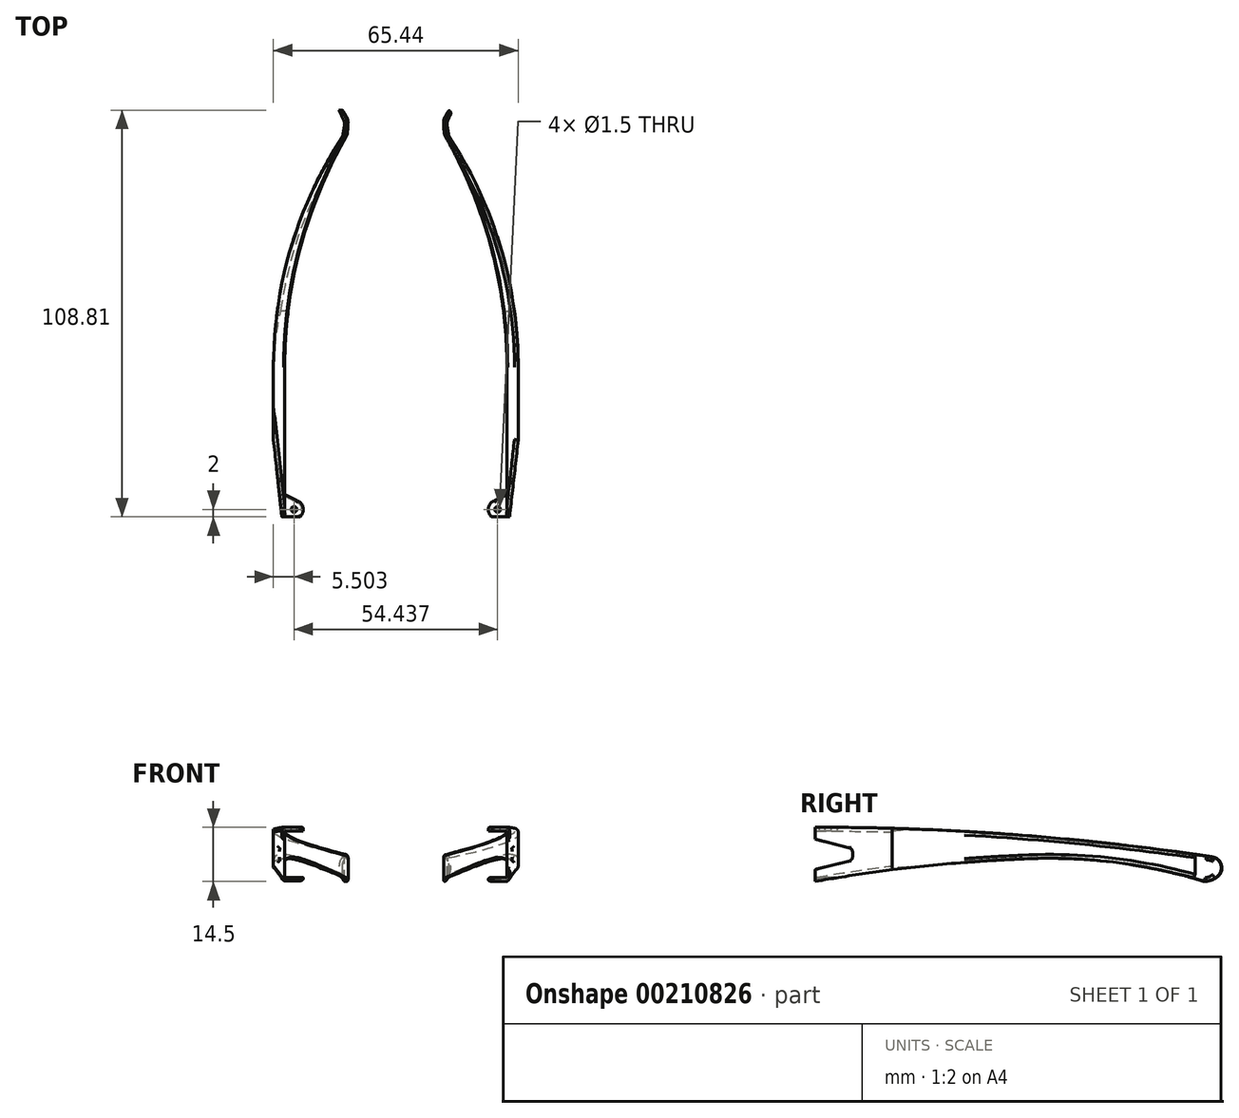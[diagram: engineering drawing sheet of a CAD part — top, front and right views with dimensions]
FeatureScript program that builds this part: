
annotation { "Feature Type Name" : "Feature", "Feature Type Description" : "" }
export const myFeature = defineFeature(function(context is Context, id is Id, definition is map)
    precondition{}
    {
        {
            var Q0;
            Q0=qCreatedBy(makeId("Top.planeOp"),FACE);
            var sketch = newSketch(context, id + "F0", { "sketchPlane" : qUnion([Q0])});
            skLineSegment(sketch, "E0.bottom", {"start": v(-10, 55) * mm, "end": v(10, 55) * mm});
            skLineSegment(sketch, "E0.top", {"start": v(-10, -55) * mm, "end": v(10, -55) * mm});
            skLineSegment(sketch, "E0.left", {"start": v(-10, 55) * mm, "end": v(-10, -55) * mm});
            skLineSegment(sketch, "E0.right", {"start": v(10, 55) * mm, "end": v(10, -55) * mm});
            skPoint(sketch, "E0.middle", {"position": v(0, 0) * mm});
            skSolve(sketch);
        }
        {
            var Q0;
            Q0=makeQuery(id+"F0.imprint","IMPRINT",FACE,{"disambiguationData":[TD([[makeQuery(id+"F0.imprint","IMPRINT",EDGE,{"derivedFrom":sQuery(id+"F0.wireOp",EDGE,"E0.bottom")}),-1.0]])]});
            extrude(context, id + "F1", {"entities" : qUnion([Q0]), "depth" : 14.5 * mm});
        }
        {
            var Q0;
            Q0=makeQuery(id+"F1.opExtrude","SWEPT_FACE",FACE,{"disambiguationData":[OSD([sQuery(id+"F0.wireOp",EDGE,"E0.right")])]});
            var sketch = newSketch(context, id + "F2", { "sketchPlane" : qUnion([Q0])});
            skLineSegment(sketch, "E1", {"start": v(-55, 14.5) * mm, "end": v(-55, 11.3) * mm});
            skLineSegment(sketch, "E2", {"start": v(-55, 0) * mm, "end": v(-55, 3.2) * mm});
            skLineSegment(sketch, "E3", {"start": v(-44.97, 6.5) * mm, "end": v(-44.97, 7.97) * mm});
            skLineSegment(sketch, "E4", {"start": v(-45.72, 8.93) * mm, "end": v(-55, 11.3) * mm});
            skLineSegment(sketch, "E5", {"start": v(-45.73, 5.52) * mm, "end": v(-55, 3.2) * mm});
            skPoint(sketch, "E6.visualSharp", {"position": v(-44.97, 8.74) * mm});
            skArc(sketch, "E6.filletArc", {"start": v(-44.97, 7.97) * mm, "mid": v(-45.18, 8.58) * mm, "end": v(-45.72, 8.93) * mm});
            skPoint(sketch, "E7.visualSharp", {"position": v(-44.97, 5.71) * mm});
            skArc(sketch, "E7.filletArc", {"start": v(-45.73, 5.52) * mm, "mid": v(-45.18, 5.88) * mm, "end": v(-44.97, 6.5) * mm});
            skLineSegment(sketch, "E8", {"start": v(55, 0) * mm, "end": v(55, 6) * mm});
            skLineSegment(sketch, "E9", {"start": v(55, 14.5) * mm, "end": v(55, 0) * mm});
            skLineSegment(sketch, "E10", {"start": v(55, 0) * mm, "end": v(49, 0) * mm});
            skArc(sketch, "E11", {"start": v(49, 0) * mm, "mid": v(50.9, 0.31) * mm, "end": v(52.62, 1.21) * mm});
            skArc(sketch, "E12", {"start": v(51.25, 6.57) * mm, "mid": v(-1.73, 12.52) * mm, "end": v(-55, 14.5) * mm});
            skPoint(sketch, "E13.endSnap0", {"position": v(0, 0) * mm});
            skArc(sketch, "E14", {"start": v(0, 6) * mm, "mid": v(-27.6, 3.9) * mm, "end": v(-55, 0) * mm});
            skArc(sketch, "E15", {"start": v(49, 0) * mm, "mid": v(24.76, 5.15) * mm, "end": v(0, 6) * mm});
            skPoint(sketch, "E16.visualSharp", {"position": v(55, 6) * mm});
            skArc(sketch, "E16.filletArc", {"start": v(52.62, 1.21) * mm, "mid": v(53.72, 4.34) * mm, "end": v(51.25, 6.57) * mm});
            skLineSegment(sketch, "E17", {"start": v(-55, 11.3) * mm, "end": v(-55, 3.2) * mm});
            skLineSegment(sketch, "E18", {"start": v(-55, 14.5) * mm, "end": v(55, 14.5) * mm});
            skSolve(sketch);
        }
        {
            var Q0;
            {var subQ0=sQuery(id+"F2.wireOp",EDGE,"E14");Q0=makeQuery(id+"F2.imprint","IMPRINT",FACE,{"disambiguationData":[TD([[makeQuery(id+"F2.imprint","IMPRINT",EDGE,{"derivedFrom":subQ0}),1.0]])]});}
            extrude(context, id + "F3", {"entities" : qUnion([Q0]), "operationType" : NewBodyOperationType.REMOVE, "oppositeDirection" : true, "depth" : 25 * mm});
        }
        {
            var Q0;
            Q0=makeQuery(id+"F2.imprint","IMPRINT",FACE,{"disambiguationData":[TD([[makeQuery(id+"F2.imprint","IMPRINT",EDGE,{"derivedFrom":sQuery(id+"F2.wireOp",EDGE,"E3")}),1.0]])]});
            extrude(context, id + "F4", {"entities" : qUnion([Q0]), "operationType" : NewBodyOperationType.REMOVE, "oppositeDirection" : true, "depth" : 25 * mm});
        }
        {
            var Q0;
            {var subQ0=sQuery(id+"F2.wireOp",EDGE,"E10");Q0=makeQuery(id+"F2.imprint","IMPRINT",FACE,{"disambiguationData":[TD([[makeQuery(id+"F2.imprint","IMPRINT",EDGE,{"derivedFrom":subQ0}),-1.0]])]});}
            extrude(context, id + "F5", {"entities" : qUnion([Q0]), "operationType" : NewBodyOperationType.REMOVE, "oppositeDirection" : true, "depth" : 25 * mm});
        }
        {
            var Q0;
            Q0=qCreatedBy(makeId("Top.planeOp"),FACE);
            var Q1;
            Q1=sQuery(id+"F2.wireOp",VERTEX,"E12.end");
            cPlane(context, id + "F6", {"entities" : qUnion([Q0, Q1]), "cplaneType" : CPlaneType.PLANE_POINT, "offset" : 25 * mm, "width" : 150 * mm, "height" : 150 * mm});
        }
        {
            var Q0;
            Q0=qCreatedBy(id+"F6.planeOp",FACE);
            var sketch = newSketch(context, id + "F7", { "sketchPlane" : qUnion([Q0])});
            skLineSegment(sketch, "E19.0", {"start": v(-10, 53.8) * mm, "end": v(-10, -55) * mm});
            skLineSegment(sketch, "E20.0", {"start": v(10, -55) * mm, "end": v(10, 55) * mm});
            skLineSegment(sketch, "E21", {"start": v(10, -55) * mm, "end": v(10, -15) * mm});
            skArc(sketch, "E22", {"start": v(10, -15) * mm, "mid": v(5.28, 17.16) * mm, "end": v(-8.48, 46.61) * mm});
            skLineSegment(sketch, "E23", {"start": v(10, -55) * mm, "end": v(7, -55) * mm});
            skLineSegment(sketch, "E24", {"start": v(7, -55) * mm, "end": v(7, -15) * mm});
            skArc(sketch, "E25", {"start": v(7, -15) * mm, "mid": v(2.83, 16.88) * mm, "end": v(-9.4, 46.62) * mm});
            skLineSegment(sketch, "E26", {"start": v(-9.94, 50.34) * mm, "end": v(-9.8, 47.93) * mm});
            skPoint(sketch, "E27.visualSharp", {"position": v(-9.75, 47.22) * mm});
            skArc(sketch, "E27.filletArc", {"start": v(-9.8, 47.93) * mm, "mid": v(-9.67, 47.25) * mm, "end": v(-9.4, 46.62) * mm});
            skLineSegment(sketch, "E28", {"start": v(-10, 53.8) * mm, "end": v(10, 53.8) * mm});
            skLineSegment(sketch, "E29", {"start": v(-10, 53.8) * mm, "end": v(-8.5, 53.8) * mm});
            skLineSegment(sketch, "E30", {"start": v(-8.5, 53.8) * mm, "end": v(-9.54, 52.04) * mm});
            skPoint(sketch, "E31.visualSharp", {"position": v(-10, 51.25) * mm});
            skArc(sketch, "E31.filletArc", {"start": v(-9.54, 52.04) * mm, "mid": v(-9.87, 51.22) * mm, "end": v(-9.94, 50.34) * mm});
            skLineSegment(sketch, "E32", {"start": v(-8.5, 53.8) * mm, "end": v(-7.5, 53.8) * mm});
            skLineSegment(sketch, "E33", {"start": v(-7.5, 53.8) * mm, "end": v(-8.7, 51.33) * mm});
            skLineSegment(sketch, "E34", {"start": v(-8.97, 49.52) * mm, "end": v(-8.48, 46.61) * mm});
            skPoint(sketch, "E35.visualSharp", {"position": v(-9.13, 50.47) * mm});
            skArc(sketch, "E35.filletArc", {"start": v(-8.7, 51.33) * mm, "mid": v(-8.98, 50.45) * mm, "end": v(-8.97, 49.52) * mm});
            skLineSegment(sketch, "E36.0.0", {"start": v(-10, 51.25) * mm, "end": v(-10, -55) * mm});
            skLineSegment(sketch, "E36.0.1", {"start": v(-10, -55) * mm, "end": v(10, -55) * mm});
            skLineSegment(sketch, "E36.0.2", {"start": v(10, -55) * mm, "end": v(10, 51.25) * mm});
            skSolve(sketch);
        }
        {
            var Q0;
            {var subQ0=sQuery(id+"F7.wireOp",EDGE,"E22");Q0=makeQuery(id+"F7.imprint","IMPRINT",FACE,{"disambiguationData":[TD([[makeQuery(id+"F7.imprint","IMPRINT",EDGE,{"derivedFrom":subQ0}),-1.0]])]});}
            extrude(context, id + "F8", {"entities" : qUnion([Q0]), "operationType" : NewBodyOperationType.REMOVE, "oppositeDirection" : true, "depth" : 25 * mm});
        }
        {
            var Q0;
            Q0=makeQuery(id+"F7.imprint","IMPRINT",FACE,{"disambiguationData":[TD([[makeQuery(id+"F7.imprint","IMPRINT",EDGE,{"derivedFrom":sQuery(id+"F7.wireOp",EDGE,"E19.0")}),1.0]])]});
            extrude(context, id + "F9", {"entities" : qUnion([Q0]), "operationType" : NewBodyOperationType.REMOVE, "oppositeDirection" : true, "depth" : 25 * mm});
        }
        {
            var Q0;
            Q0=qCreatedBy(makeId("Top.planeOp"),FACE);
            var sketch = newSketch(context, id + "F10", { "sketchPlane" : qUnion([Q0])});
            skArc(sketch, "E37.0", {"start": v(3.71, -50.63) * mm, "mid": v(2.03, -52.6) * mm, "end": v(3, -55) * mm});
            skLineSegment(sketch, "E38.0", {"start": v(3.71, -50.63) * mm, "end": v(7, -49.01) * mm});
            skLineSegment(sketch, "E39.0", {"start": v(7, -49.01) * mm, "end": v(7, -55) * mm});
            skLineSegment(sketch, "E40.0", {"start": v(3, -55) * mm, "end": v(7, -55) * mm});
            skPoint(sketch, "E41.orphan", {"position": v(-10, -55) * mm});
            skPoint(sketch, "E42.orphan", {"position": v(10, -55) * mm});
            skCircle(sketch, "E43.0", {"center": v(4.5, -53) * mm, "radius": 0.75 * mm});
            skSolve(sketch);
        }
        {
            var Q0;
            Q0=makeQuery(id+"F10.imprint","IMPRINT",FACE,{"disambiguationData":[TD([[makeQuery(id+"F10.imprint","IMPRINT",EDGE,{"derivedFrom":sQuery(id+"F10.wireOp",EDGE,"E37.0")}),1.0]])]});
            extrude(context, id + "F11", {"entities" : qUnion([Q0]), "operationType" : NewBodyOperationType.ADD, "depth" : 1 * mm});
        }
        {
            var Q0;
            {var subQ0=sQuery(id+"F2.wireOp",EDGE,"E14");Q0=makeQuery(id+"F2.imprint","IMPRINT",FACE,{"disambiguationData":[TD([[makeQuery(id+"F2.imprint","IMPRINT",EDGE,{"derivedFrom":subQ0}),1.0]])]});}
            extrude(context, id + "F12", {"entities" : qUnion([Q0]), "operationType" : NewBodyOperationType.REMOVE, "oppositeDirection" : true, "depth" : 25 * mm});
        }
        {
            var Q0;
            {var subQ0=sQuery(id+"F2.wireOp",EDGE,"E10");Q0=makeQuery(id+"F2.imprint","IMPRINT",FACE,{"disambiguationData":[TD([[makeQuery(id+"F2.imprint","IMPRINT",EDGE,{"derivedFrom":subQ0}),-1.0]])]});}
            extrude(context, id + "F13", {"entities" : qUnion([Q0]), "operationType" : NewBodyOperationType.REMOVE, "oppositeDirection" : true, "depth" : 25 * mm});
        }
        {
            var Q0;
            Q0=qCreatedBy(makeId("Top.planeOp"),FACE);
            var Q1;
            Q1=sQuery(id+"F7.wireOp",VERTEX,"E24.start");
            cPlane(context, id + "F14", {"entities" : qUnion([Q0, Q1]), "cplaneType" : CPlaneType.PLANE_POINT, "offset" : 25 * mm, "width" : 150 * mm, "height" : 150 * mm});
        }
        {
            var Q0;
            Q0=qCreatedBy(id+"F14.planeOp",FACE);
            var sketch = newSketch(context, id + "F15", { "sketchPlane" : qUnion([Q0])});
            skLineSegment(sketch, "E44.0", {"start": v(7, -55) * mm, "end": v(7, -49.01) * mm});
            skLineSegment(sketch, "E45.0", {"start": v(3.71, -50.63) * mm, "end": v(7, -49.01) * mm});
            skArc(sketch, "E46.0", {"start": v(3.71, -50.63) * mm, "mid": v(2.03, -52.6) * mm, "end": v(3, -55) * mm});
            skCircle(sketch, "E47.0", {"center": v(4.5, -53) * mm, "radius": 0.75 * mm});
            skLineSegment(sketch, "E48.0", {"start": v(3, -55) * mm, "end": v(7, -55) * mm});
            skPoint(sketch, "E49.orphan", {"position": v(6.85, -49.09) * mm});
            skPoint(sketch, "E50.orphan", {"position": v(7, -15) * mm});
            skPoint(sketch, "E51.orphan", {"position": v(-10, -55) * mm});
            skPoint(sketch, "E52.orphan", {"position": v(10, -55) * mm});
            skSolve(sketch);
        }
        {
            var Q0;
            Q0=makeQuery(id+"F15.imprint","IMPRINT",FACE,{"disambiguationData":[TD([[makeQuery(id+"F15.imprint","IMPRINT",EDGE,{"derivedFrom":sQuery(id+"F15.wireOp",EDGE,"E44.0")}),1.0]])]});
            extrude(context, id + "F16", {"entities" : qUnion([Q0]), "operationType" : NewBodyOperationType.ADD, "oppositeDirection" : true, "depth" : 1 * mm});
        }
        {
            var Q0;
            Q0=makeQuery(id+"F1.opExtrude","SWEPT_BODY",BODY,{"disambiguationData":[OSD([sQuery(id+"F0.wireOp",EDGE,"E0.bottom"),sQuery(id+"F0.wireOp",EDGE,"E0.top"),sQuery(id+"F0.wireOp",EDGE,"E0.left"),sQuery(id+"F0.wireOp",EDGE,"E0.right")])]});
            transform(context, id + "F17", {"entities" : qUnion([Q0]), "transformType" : TransformType.TRANSLATION_3D, "dx" : 0 * mm, "dy" : 0 * mm, "dz" : 0 * mm, "makeCopy" : true});
        }
        {
            var Q0;
            Q0=makeQuery(id+"F17.opPattern","COPY",BODY,{"derivedFrom":makeQuery(id+"F1.opExtrude","SWEPT_BODY",BODY,{"disambiguationData":[OSD([sQuery(id+"F0.wireOp",EDGE,"E0.bottom"),sQuery(id+"F0.wireOp",EDGE,"E0.top"),sQuery(id+"F0.wireOp",EDGE,"E0.left"),sQuery(id+"F0.wireOp",EDGE,"E0.right")])]}),"instanceName":"1"});
            deleteBodies(context, id + "F18", {"entities" : qUnion([Q0])});
        }
        {
            var Q0;
            {var subQ0=sQuery(id+"F7.wireOp",EDGE,"E22");Q0=makeQuery(id+"F7.imprint","IMPRINT",FACE,{"disambiguationData":[TD([[makeQuery(id+"F7.imprint","IMPRINT",EDGE,{"derivedFrom":subQ0}),1.0]])]});}
            var sketch = newSketch(context, id + "F19", { "sketchPlane" : qUnion([Q0])});
            skLineSegment(sketch, "E53.0", {"start": v(-10, -55) * mm, "end": v(10, -55) * mm});
            skLineSegment(sketch, "E54.0", {"start": v(7, -55) * mm, "end": v(7, -15) * mm});
            skLineSegment(sketch, "E55", {"start": v(7, -55) * mm, "end": v(7.7, -55) * mm});
            skLineSegment(sketch, "E56.0", {"start": v(10, -34.38) * mm, "end": v(10, -55) * mm});
            skLineSegment(sketch, "E57", {"start": v(7.7, -55) * mm, "end": v(10, -34.38) * mm});
            skPoint(sketch, "E58.orphan", {"position": v(10, 51.25) * mm});
            skSolve(sketch);
        }
        {
            var Q0;
            Q0 = qSketchRegion(id + "F19", true);
            extrude(context, id + "F20", {"entities" : qUnion([Q0]), "operationType" : NewBodyOperationType.REMOVE, "oppositeDirection" : true, "depth" : 25 * mm});
        }
        {
            var Q0;
            Q0=qCreatedBy(makeId("Top.planeOp"),FACE);
            var sketch = newSketch(context, id + "F21", { "sketchPlane" : qUnion([Q0])});
            skLineSegment(sketch, "E59", {"start": v(-22.72, 54.97) * mm, "end": v(-22.72, -56.62) * mm});
            skSolve(sketch);
        }
        {
            var Q0;
            Q0=qCreatedBy(makeId("Right.planeOp"),FACE);
            var Q1;
            Q1=sQuery(id+"F21.wireOp",VERTEX,"E59.end");
            cPlane(context, id + "F22", {"entities" : qUnion([Q0, Q1]), "cplaneType" : CPlaneType.PLANE_POINT, "offset" : 25 * mm, "width" : 150 * mm, "height" : 150 * mm});
        }
        {
            var Q0;
            Q0=makeQuery(id+"F1.opExtrude","SWEPT_BODY",BODY,{"disambiguationData":[OSD([sQuery(id+"F0.wireOp",EDGE,"E0.bottom"),sQuery(id+"F0.wireOp",EDGE,"E0.top"),sQuery(id+"F0.wireOp",EDGE,"E0.left"),sQuery(id+"F0.wireOp",EDGE,"E0.right")])]});
            var Q1;
            Q1=qCreatedBy(id+"F22.planeOp",FACE);
            mirror(context, id + "F23", {"entities" : qUnion([Q0]), "mirrorPlane" : qUnion([Q1])});
        }
        {
            var Q0;
            Q0=makeQuery(id+"F20.boolean.opBoolean","INTERSECT",EDGE,{"derivedFrom":[makeQuery(id+"F5.boolean.opBoolean","COPY",FACE,{"derivedFrom":makeQuery(id+"F5.opExtrude","SWEPT_FACE",FACE,{"disambiguationData":[OSD([sQuery(id+"F2.wireOp",EDGE,"E12")])]})}),makeQuery(id+"F20.opExtrude","SWEPT_FACE",FACE,{"disambiguationData":[OSD([sQuery(id+"F19.wireOp",EDGE,"E57")])]})]});
            var Q1;
            Q1=makeQuery(id+"F5.boolean.opBoolean","COPY",EDGE,{"derivedFrom":makeQuery(id+"F5.opExtrude","CAP_EDGE",EDGE,{"disambiguationData":[OSD([sQuery(id+"F2.wireOp",EDGE,"E12")])],"isStart":true})});
            var Q2;
            Q2=makeQuery(id+"F8.boolean.opBoolean","INTERSECT",EDGE,{"derivedFrom":[makeQuery(id+"F5.boolean.opBoolean","COPY",FACE,{"derivedFrom":makeQuery(id+"F5.opExtrude","SWEPT_FACE",FACE,{"disambiguationData":[OSD([sQuery(id+"F2.wireOp",EDGE,"E12")])]})}),makeQuery(id+"F8.opExtrude","SWEPT_FACE",FACE,{"disambiguationData":[OSD([sQuery(id+"F7.wireOp",EDGE,"E22")])]})]});
            var Q3;
            {var subQ0=sQuery(id+"F2.wireOp",EDGE,"E14");Q3=makeQuery(id+"F20.boolean.opBoolean","INTERSECT",EDGE,{"derivedFrom":[makeQuery(id+"F12.boolean.opBoolean","MERGE",FACE,{"derivedFrom":[makeQuery(id+"F3.boolean.opBoolean","COPY",FACE,{"derivedFrom":makeQuery(id+"F3.opExtrude","SWEPT_FACE",FACE,{"disambiguationData":[OSD([subQ0])]})}),makeQuery(id+"F12.opExtrude","SWEPT_FACE",FACE,{"disambiguationData":[OSD([subQ0])]})]}),makeQuery(id+"F20.opExtrude","SWEPT_FACE",FACE,{"disambiguationData":[OSD([sQuery(id+"F19.wireOp",EDGE,"E57")])]})]});}
            var Q4;
            Q4=makeQuery(id+"F3.boolean.opBoolean","COPY",EDGE,{"derivedFrom":makeQuery(id+"F3.opExtrude","CAP_EDGE",EDGE,{"disambiguationData":[OSD([sQuery(id+"F2.wireOp",EDGE,"E14")])],"isStart":true})});
            var Q5;
            Q5=makeQuery(id+"F8.boolean.opBoolean","INTERSECT",EDGE,{"derivedFrom":[makeQuery(id+"F3.boolean.opBoolean","COPY",FACE,{"derivedFrom":makeQuery(id+"F3.opExtrude","SWEPT_FACE",FACE,{"disambiguationData":[OSD([sQuery(id+"F2.wireOp",EDGE,"E14")])]})}),makeQuery(id+"F8.opExtrude","SWEPT_FACE",FACE,{"disambiguationData":[OSD([sQuery(id+"F7.wireOp",EDGE,"E22")])]})]});
            var Q6;
            Q6=makeQuery(id+"F8.boolean.opBoolean","INTERSECT",EDGE,{"derivedFrom":[makeQuery(id+"F3.boolean.opBoolean","COPY",FACE,{"derivedFrom":makeQuery(id+"F3.opExtrude","SWEPT_FACE",FACE,{"disambiguationData":[OSD([sQuery(id+"F2.wireOp",EDGE,"E15")])]})}),makeQuery(id+"F8.opExtrude","SWEPT_FACE",FACE,{"disambiguationData":[OSD([sQuery(id+"F7.wireOp",EDGE,"E22")])]})]});
            var Q7;
            Q7=makeQuery(id+"F8.boolean.opBoolean","INTERSECT",EDGE,{"derivedFrom":[makeQuery(id+"F3.boolean.opBoolean","COPY",FACE,{"derivedFrom":makeQuery(id+"F3.opExtrude","SWEPT_FACE",FACE,{"disambiguationData":[OSD([sQuery(id+"F2.wireOp",EDGE,"E15")])]})}),makeQuery(id+"F8.opExtrude","SWEPT_FACE",FACE,{"disambiguationData":[OSD([sQuery(id+"F7.wireOp",EDGE,"E34")])]})]});
            var Q8;
            Q8=makeQuery(id+"F8.boolean.opBoolean","INTERSECT",EDGE,{"derivedFrom":[makeQuery(id+"F5.boolean.opBoolean","COPY",FACE,{"derivedFrom":makeQuery(id+"F5.opExtrude","SWEPT_FACE",FACE,{"disambiguationData":[OSD([sQuery(id+"F2.wireOp",EDGE,"E11")])]})}),makeQuery(id+"F8.opExtrude","SWEPT_FACE",FACE,{"disambiguationData":[OSD([sQuery(id+"F7.wireOp",EDGE,"E34")])]})]});
            var Q9;
            Q9=makeQuery(id+"F8.boolean.opBoolean","INTERSECT",EDGE,{"derivedFrom":[makeQuery(id+"F5.boolean.opBoolean","COPY",FACE,{"derivedFrom":makeQuery(id+"F5.opExtrude","SWEPT_FACE",FACE,{"disambiguationData":[OSD([sQuery(id+"F2.wireOp",EDGE,"E11")])]})}),makeQuery(id+"F8.opExtrude","SWEPT_FACE",FACE,{"disambiguationData":[OSD([sQuery(id+"F7.wireOp",EDGE,"E35.filletArc")])]})]});
            fillet(context, id + "F24", {"entities" : qUnion([Q0, Q1, Q2, Q3, Q4, Q5, Q6, Q7, Q8, Q9]), "radius" : 1 * mm, "tangentPropagation" : true, "allowEdgeOverflow" : false});
        }
        {
            var Q0;
            {var subQ0=makeQuery(id+"F9.opExtrude","SWEPT_FACE",FACE,{"disambiguationData":[OSD([sQuery(id+"F7.wireOp",EDGE,"E24")])]});var subQ1=makeQuery(id+"F5.boolean.opBoolean","COPY",FACE,{"derivedFrom":makeQuery(id+"F5.opExtrude","SWEPT_FACE",FACE,{"disambiguationData":[OSD([sQuery(id+"F2.wireOp",EDGE,"E12")])]})});Q0=makeQuery(id+"F16.boolean.opBoolean","SPLIT",EDGE,{"disambiguationData":[TD([makeQuery(id+"F9.boolean.opBoolean","COPY",FACE,{"derivedFrom":makeQuery(id+"F9.opExtrude","SWEPT_FACE",FACE,{"disambiguationData":[OSD([sQuery(id+"F7.wireOp",EDGE,"E25")])]})})])],"derivedFrom":makeQuery(id+"F9.boolean.opBoolean","INTERSECT",EDGE,{"derivedFrom":[subQ1,subQ0]})});}
            fillet(context, id + "F25", {"entities" : qUnion([Q0]), "radius" : 0.2 * mm, "tangentPropagation" : true, "allowEdgeOverflow" : false});
        }
        {
            var Q0;
            {var subQ1=makeQuery(id+"F9.opExtrude","SWEPT_FACE",FACE,{"disambiguationData":[OSD([sQuery(id+"F7.wireOp",EDGE,"E24")])]});var subQ2=makeQuery(id+"F3.boolean.opBoolean","COPY",FACE,{"derivedFrom":makeQuery(id+"F3.opExtrude","SWEPT_FACE",FACE,{"disambiguationData":[OSD([sQuery(id+"F2.wireOp",EDGE,"E14")])]})});Q0=makeQuery(id+"F11.boolean.opBoolean","SPLIT",EDGE,{"disambiguationData":[TD([makeQuery(id+"F9.boolean.opBoolean","COPY",FACE,{"derivedFrom":makeQuery(id+"F9.opExtrude","SWEPT_FACE",FACE,{"disambiguationData":[OSD([sQuery(id+"F7.wireOp",EDGE,"E25")])]})})])],"derivedFrom":makeQuery(id+"F9.boolean.opBoolean","INTERSECT",EDGE,{"derivedFrom":[subQ2,subQ1]})});}
            var Q1;
            Q1=makeQuery(id+"F9.boolean.opBoolean","INTERSECT",EDGE,{"derivedFrom":[makeQuery(id+"F3.boolean.opBoolean","COPY",FACE,{"derivedFrom":makeQuery(id+"F3.opExtrude","SWEPT_FACE",FACE,{"disambiguationData":[OSD([sQuery(id+"F2.wireOp",EDGE,"E14")])]})}),makeQuery(id+"F9.opExtrude","SWEPT_FACE",FACE,{"disambiguationData":[OSD([sQuery(id+"F7.wireOp",EDGE,"E25")])]})]});
            var Q2;
            Q2=makeQuery(id+"F9.boolean.opBoolean","INTERSECT",EDGE,{"derivedFrom":[makeQuery(id+"F3.boolean.opBoolean","COPY",FACE,{"derivedFrom":makeQuery(id+"F3.opExtrude","SWEPT_FACE",FACE,{"disambiguationData":[OSD([sQuery(id+"F2.wireOp",EDGE,"E15")])]})}),makeQuery(id+"F9.opExtrude","SWEPT_FACE",FACE,{"disambiguationData":[OSD([sQuery(id+"F7.wireOp",EDGE,"E25")])]})]});
            var Q3;
            Q3=makeQuery(id+"F24.opFillet","BLEND_EDGE",EDGE,{"blendedFrom":[makeQuery(id+"F8.boolean.opBoolean","INTERSECT",EDGE,{"derivedFrom":[makeQuery(id+"F3.boolean.opBoolean","COPY",FACE,{"derivedFrom":makeQuery(id+"F3.opExtrude","SWEPT_FACE",FACE,{"disambiguationData":[OSD([sQuery(id+"F2.wireOp",EDGE,"E15")])]})}),makeQuery(id+"F8.opExtrude","SWEPT_FACE",FACE,{"disambiguationData":[OSD([sQuery(id+"F7.wireOp",EDGE,"E22")])]})]}),makeQuery(id+"F9.boolean.opBoolean","COPY",FACE,{"derivedFrom":makeQuery(id+"F9.opExtrude","SWEPT_FACE",FACE,{"disambiguationData":[OSD([sQuery(id+"F7.wireOp",EDGE,"E25")])]})})],"blendedInto":[makeQuery(id+"F9.boolean.opBoolean","COPY",FACE,{"derivedFrom":makeQuery(id+"F9.opExtrude","SWEPT_FACE",FACE,{"disambiguationData":[OSD([sQuery(id+"F7.wireOp",EDGE,"E25")])]})})]});
            var Q4;
            Q4=makeQuery(id+"F24.opFillet","BLEND_EDGE",EDGE,{"blendedFrom":[makeQuery(id+"F8.boolean.opBoolean","INTERSECT",EDGE,{"derivedFrom":[makeQuery(id+"F3.boolean.opBoolean","COPY",FACE,{"derivedFrom":makeQuery(id+"F3.opExtrude","SWEPT_FACE",FACE,{"disambiguationData":[OSD([sQuery(id+"F2.wireOp",EDGE,"E15")])]})}),makeQuery(id+"F8.opExtrude","SWEPT_FACE",FACE,{"disambiguationData":[OSD([sQuery(id+"F7.wireOp",EDGE,"E34")])]})]}),makeQuery(id+"F9.boolean.opBoolean","COPY",FACE,{"derivedFrom":makeQuery(id+"F9.opExtrude","SWEPT_FACE",FACE,{"disambiguationData":[OSD([sQuery(id+"F7.wireOp",EDGE,"E25")])]})})],"blendedInto":[makeQuery(id+"F9.boolean.opBoolean","COPY",FACE,{"derivedFrom":makeQuery(id+"F9.opExtrude","SWEPT_FACE",FACE,{"disambiguationData":[OSD([sQuery(id+"F7.wireOp",EDGE,"E25")])]})})]});
            var Q5;
            Q5=makeQuery(id+"F24.opFillet","BLEND_EDGE",EDGE,{"disambiguationData":[OD(1.0)],"blendedFrom":[makeQuery(id+"F8.boolean.opBoolean","INTERSECT",EDGE,{"derivedFrom":[makeQuery(id+"F5.boolean.opBoolean","COPY",FACE,{"derivedFrom":makeQuery(id+"F5.opExtrude","SWEPT_FACE",FACE,{"disambiguationData":[OSD([sQuery(id+"F2.wireOp",EDGE,"E11")])]})}),makeQuery(id+"F8.opExtrude","SWEPT_FACE",FACE,{"disambiguationData":[OSD([sQuery(id+"F7.wireOp",EDGE,"E34")])]})]}),makeQuery(id+"F9.boolean.opBoolean","COPY",FACE,{"derivedFrom":makeQuery(id+"F9.opExtrude","SWEPT_FACE",FACE,{"disambiguationData":[OSD([sQuery(id+"F7.wireOp",EDGE,"E26")])]})})],"blendedInto":[makeQuery(id+"F9.boolean.opBoolean","COPY",FACE,{"derivedFrom":makeQuery(id+"F9.opExtrude","SWEPT_FACE",FACE,{"disambiguationData":[OSD([sQuery(id+"F7.wireOp",EDGE,"E26")])]})})]});
            var Q6;
            Q6=makeQuery(id+"F24.opFillet","BLEND_EDGE",EDGE,{"blendedFrom":[makeQuery(id+"F8.boolean.opBoolean","INTERSECT",EDGE,{"derivedFrom":[makeQuery(id+"F5.boolean.opBoolean","COPY",FACE,{"derivedFrom":makeQuery(id+"F5.opExtrude","SWEPT_FACE",FACE,{"disambiguationData":[OSD([sQuery(id+"F2.wireOp",EDGE,"E11")])]})}),makeQuery(id+"F8.opExtrude","SWEPT_FACE",FACE,{"disambiguationData":[OSD([sQuery(id+"F7.wireOp",EDGE,"E34")])]})]}),makeQuery(id+"F9.boolean.opBoolean","COPY",FACE,{"derivedFrom":makeQuery(id+"F9.opExtrude","SWEPT_FACE",FACE,{"disambiguationData":[OSD([sQuery(id+"F7.wireOp",EDGE,"E31.filletArc")])]})})],"blendedInto":[makeQuery(id+"F9.boolean.opBoolean","COPY",FACE,{"derivedFrom":makeQuery(id+"F9.opExtrude","SWEPT_FACE",FACE,{"disambiguationData":[OSD([sQuery(id+"F7.wireOp",EDGE,"E31.filletArc")])]})})]});
            fillet(context, id + "F26", {"entities" : qUnion([Q0, Q1, Q2, Q3, Q4, Q5, Q6]), "radius" : 0.2 * mm, "tangentPropagation" : true, "allowEdgeOverflow" : false});
        }
        {
            var Q0;
            Q0=makeQuery(id+"F9.boolean.opBoolean","INTERSECT",EDGE,{"derivedFrom":[makeQuery(id+"F4.boolean.opBoolean","COPY",FACE,{"derivedFrom":makeQuery(id+"F4.opExtrude","SWEPT_FACE",FACE,{"disambiguationData":[OSD([sQuery(id+"F2.wireOp",EDGE,"E5")])]})}),makeQuery(id+"F9.opExtrude","SWEPT_FACE",FACE,{"disambiguationData":[OSD([sQuery(id+"F7.wireOp",EDGE,"E24")])]})]});
            var Q1;
            Q1=makeQuery(id+"F20.boolean.opBoolean","INTERSECT",EDGE,{"derivedFrom":[makeQuery(id+"F4.boolean.opBoolean","COPY",FACE,{"derivedFrom":makeQuery(id+"F4.opExtrude","SWEPT_FACE",FACE,{"disambiguationData":[OSD([sQuery(id+"F2.wireOp",EDGE,"E5")])]})}),makeQuery(id+"F20.opExtrude","SWEPT_FACE",FACE,{"disambiguationData":[OSD([sQuery(id+"F19.wireOp",EDGE,"E57")])]})]});
            var Q2;
            Q2=makeQuery(id+"F11.opExtrude","CAP_EDGE",EDGE,{"disambiguationData":[OSD([sQuery(id+"F10.wireOp",EDGE,"E38.0")])],"isStart":false});
            var Q3;
            Q3=makeQuery(id+"F11.opExtrude","CAP_EDGE",EDGE,{"disambiguationData":[OSD([sQuery(id+"F10.wireOp",EDGE,"E37.0")])],"isStart":false});
            var Q4;
            Q4=makeQuery(id+"F16.opExtrude","CAP_EDGE",EDGE,{"disambiguationData":[OSD([sQuery(id+"F15.wireOp",EDGE,"E45.0")])],"isStart":true});
            var Q5;
            Q5=makeQuery(id+"F16.opExtrude","CAP_EDGE",EDGE,{"disambiguationData":[OSD([sQuery(id+"F15.wireOp",EDGE,"E46.0")])],"isStart":true});
            fillet(context, id + "F27", {"entities" : qUnion([Q0, Q1, Q2, Q3, Q4, Q5]), "radius" : 0.5 * mm, "tangentPropagation" : true, "allowEdgeOverflow" : false});
        }
        {
            var Q0;
            Q0=makeQuery(id+"F23.opPattern","COPY",EDGE,{"derivedFrom":makeQuery(id+"F20.boolean.opBoolean","INTERSECT",EDGE,{"derivedFrom":[makeQuery(id+"F5.boolean.opBoolean","COPY",FACE,{"derivedFrom":makeQuery(id+"F5.opExtrude","SWEPT_FACE",FACE,{"disambiguationData":[OSD([sQuery(id+"F2.wireOp",EDGE,"E12")])]})}),makeQuery(id+"F20.opExtrude","SWEPT_FACE",FACE,{"disambiguationData":[OSD([sQuery(id+"F19.wireOp",EDGE,"E57")])]})]}),"instanceName":"1"});
            var Q1;
            Q1=makeQuery(id+"F23.opPattern","COPY",EDGE,{"derivedFrom":makeQuery(id+"F5.boolean.opBoolean","COPY",EDGE,{"derivedFrom":makeQuery(id+"F5.opExtrude","CAP_EDGE",EDGE,{"disambiguationData":[OSD([sQuery(id+"F2.wireOp",EDGE,"E12")])],"isStart":true})}),"instanceName":"1"});
            var Q2;
            Q2=makeQuery(id+"F23.opPattern","COPY",EDGE,{"derivedFrom":makeQuery(id+"F8.boolean.opBoolean","INTERSECT",EDGE,{"derivedFrom":[makeQuery(id+"F3.boolean.opBoolean","COPY",FACE,{"derivedFrom":makeQuery(id+"F3.opExtrude","SWEPT_FACE",FACE,{"disambiguationData":[OSD([sQuery(id+"F2.wireOp",EDGE,"E15")])]})}),makeQuery(id+"F8.opExtrude","SWEPT_FACE",FACE,{"disambiguationData":[OSD([sQuery(id+"F7.wireOp",EDGE,"E22")])]})]}),"instanceName":"1"});
            var Q3;
            Q3=makeQuery(id+"F23.opPattern","COPY",EDGE,{"derivedFrom":makeQuery(id+"F3.boolean.opBoolean","COPY",EDGE,{"derivedFrom":makeQuery(id+"F3.opExtrude","CAP_EDGE",EDGE,{"disambiguationData":[OSD([sQuery(id+"F2.wireOp",EDGE,"E14")])],"isStart":true})}),"instanceName":"1"});
            var Q4;
            {var subQ0=sQuery(id+"F2.wireOp",EDGE,"E14");Q4=makeQuery(id+"F23.opPattern","COPY",EDGE,{"derivedFrom":makeQuery(id+"F20.boolean.opBoolean","INTERSECT",EDGE,{"derivedFrom":[makeQuery(id+"F12.boolean.opBoolean","MERGE",FACE,{"derivedFrom":[makeQuery(id+"F3.boolean.opBoolean","COPY",FACE,{"derivedFrom":makeQuery(id+"F3.opExtrude","SWEPT_FACE",FACE,{"disambiguationData":[OSD([subQ0])]})}),makeQuery(id+"F12.opExtrude","SWEPT_FACE",FACE,{"disambiguationData":[OSD([subQ0])]})]}),makeQuery(id+"F20.opExtrude","SWEPT_FACE",FACE,{"disambiguationData":[OSD([sQuery(id+"F19.wireOp",EDGE,"E57")])]})]}),"instanceName":"1"});}
            fillet(context, id + "F28", {"entities" : qUnion([Q0, Q1, Q2, Q3, Q4]), "radius" : 1 * mm, "tangentPropagation" : true, "allowEdgeOverflow" : false});
        }
        {
            var Q0;
            Q0=makeQuery(id+"F23.opPattern","COPY",EDGE,{"derivedFrom":makeQuery(id+"F16.opExtrude","CAP_EDGE",EDGE,{"disambiguationData":[OSD([sQuery(id+"F15.wireOp",EDGE,"E48.0")])],"isStart":true}),"instanceName":"1"});
            var Q1;
            Q1=makeQuery(id+"F23.opPattern","COPY",EDGE,{"derivedFrom":makeQuery(id+"F16.opExtrude","CAP_EDGE",EDGE,{"disambiguationData":[OSD([sQuery(id+"F15.wireOp",EDGE,"E46.0")])],"isStart":true}),"instanceName":"1"});
            var Q2;
            Q2=makeQuery(id+"F23.opPattern","COPY",EDGE,{"derivedFrom":makeQuery(id+"F16.opExtrude","CAP_EDGE",EDGE,{"disambiguationData":[OSD([sQuery(id+"F15.wireOp",EDGE,"E45.0")])],"isStart":true}),"instanceName":"1"});
            var Q3;
            {var subQ0=sQuery(id+"F2.wireOp",EDGE,"E14");var subQ1=sQuery(id+"F2.wireOp",EDGE,"E2");var subQ2=sQuery(id+"F0.wireOp",EDGE,"E0.right");Q3=makeQuery(id+"F23.opPattern","COPY",EDGE,{"derivedFrom":makeQuery(id+"F12.boolean.opBoolean","MERGE",EDGE,{"derivedFrom":[makeQuery(id+"F3.boolean.opBoolean","MERGE",EDGE,{"derivedFrom":[makeQuery(id+"F1.opExtrude","CAP_EDGE",EDGE,{"disambiguationData":[OSD([sQuery(id+"F0.wireOp",EDGE,"E0.top")])],"isStart":true}),makeQuery(id+"F3.opExtrude","SWEPT_EDGE",EDGE,{"disambiguationData":[OSD([subQ2,subQ1,subQ0])]})]}),makeQuery(id+"F11.opExtrude","CAP_EDGE",EDGE,{"disambiguationData":[OSD([sQuery(id+"F10.wireOp",EDGE,"E40.0")])],"isStart":true}),makeQuery(id+"F12.opExtrude","SWEPT_EDGE",EDGE,{"disambiguationData":[OSD([subQ2,subQ1,subQ0])]})]}),"instanceName":"1"});}
            var Q4;
            Q4=makeQuery(id+"F23.opPattern","COPY",EDGE,{"derivedFrom":makeQuery(id+"F12.boolean.opBoolean","INTERSECT",EDGE,{"derivedFrom":[makeQuery(id+"F11.opExtrude","SWEPT_FACE",FACE,{"disambiguationData":[OSD([sQuery(id+"F10.wireOp",EDGE,"E37.0")])]}),makeQuery(id+"F12.opExtrude","SWEPT_FACE",FACE,{"disambiguationData":[OSD([sQuery(id+"F2.wireOp",EDGE,"E14")])]})]}),"instanceName":"1"});
            var Q5;
            Q5=makeQuery(id+"F23.opPattern","COPY",EDGE,{"derivedFrom":makeQuery(id+"F12.boolean.opBoolean","INTERSECT",EDGE,{"derivedFrom":[makeQuery(id+"F11.opExtrude","SWEPT_FACE",FACE,{"disambiguationData":[OSD([sQuery(id+"F10.wireOp",EDGE,"E38.0")])]}),makeQuery(id+"F12.opExtrude","SWEPT_FACE",FACE,{"disambiguationData":[OSD([sQuery(id+"F2.wireOp",EDGE,"E14")])]})]}),"instanceName":"1"});
            fillet(context, id + "F29", {"entities" : qUnion([Q0, Q1, Q2, Q3, Q4, Q5]), "radius" : 0.5 * mm, "tangentPropagation" : true, "allowEdgeOverflow" : false});
        }
        {
            var Q0;
            Q0=makeQuery(id+"F23.opPattern","COPY",EDGE,{"derivedFrom":makeQuery(id+"F20.boolean.opBoolean","INTERSECT",EDGE,{"derivedFrom":[makeQuery(id+"F4.boolean.opBoolean","COPY",FACE,{"derivedFrom":makeQuery(id+"F4.opExtrude","SWEPT_FACE",FACE,{"disambiguationData":[OSD([sQuery(id+"F2.wireOp",EDGE,"E4")])]})}),makeQuery(id+"F20.opExtrude","SWEPT_FACE",FACE,{"disambiguationData":[OSD([sQuery(id+"F19.wireOp",EDGE,"E57")])]})]}),"instanceName":"1"});
            var Q1;
            Q1=makeQuery(id+"F23.opPattern","COPY",EDGE,{"derivedFrom":makeQuery(id+"F20.boolean.opBoolean","INTERSECT",EDGE,{"derivedFrom":[makeQuery(id+"F4.boolean.opBoolean","COPY",FACE,{"derivedFrom":makeQuery(id+"F4.opExtrude","SWEPT_FACE",FACE,{"disambiguationData":[OSD([sQuery(id+"F2.wireOp",EDGE,"E6.filletArc")])]})}),makeQuery(id+"F20.opExtrude","SWEPT_FACE",FACE,{"disambiguationData":[OSD([sQuery(id+"F19.wireOp",EDGE,"E57")])]})]}),"instanceName":"1"});
            fillet(context, id + "F30", {"entities" : qUnion([Q0, Q1]), "radius" : 0.5 * mm, "tangentPropagation" : true, "allowEdgeOverflow" : false});
        }
        {
            var Q0;
            {var subQ0=makeQuery(id+"F9.opExtrude","SWEPT_FACE",FACE,{"disambiguationData":[OSD([sQuery(id+"F7.wireOp",EDGE,"E24")])]});var subQ1=makeQuery(id+"F5.boolean.opBoolean","COPY",FACE,{"derivedFrom":makeQuery(id+"F5.opExtrude","SWEPT_FACE",FACE,{"disambiguationData":[OSD([sQuery(id+"F2.wireOp",EDGE,"E12")])]})});Q0=makeQuery(id+"F23.opPattern","COPY",EDGE,{"derivedFrom":makeQuery(id+"F16.boolean.opBoolean","SPLIT",EDGE,{"disambiguationData":[TD([makeQuery(id+"F9.boolean.opBoolean","COPY",FACE,{"derivedFrom":makeQuery(id+"F9.opExtrude","SWEPT_FACE",FACE,{"disambiguationData":[OSD([sQuery(id+"F7.wireOp",EDGE,"E25")])]})})])],"derivedFrom":makeQuery(id+"F9.boolean.opBoolean","INTERSECT",EDGE,{"derivedFrom":[subQ1,subQ0]})}),"instanceName":"1"});}
            var Q1;
            Q1=makeQuery(id+"F23.opPattern","COPY",EDGE,{"derivedFrom":makeQuery(id+"F9.boolean.opBoolean","INTERSECT",EDGE,{"derivedFrom":[makeQuery(id+"F5.boolean.opBoolean","COPY",FACE,{"derivedFrom":makeQuery(id+"F5.opExtrude","SWEPT_FACE",FACE,{"disambiguationData":[OSD([sQuery(id+"F2.wireOp",EDGE,"E12")])]})}),makeQuery(id+"F9.opExtrude","SWEPT_FACE",FACE,{"disambiguationData":[OSD([sQuery(id+"F7.wireOp",EDGE,"E25")])]})]}),"instanceName":"1"});
            var Q2;
            Q2=makeQuery(id+"F23.opPattern","COPY",EDGE,{"derivedFrom":makeQuery(id+"F9.boolean.opBoolean","INTERSECT",EDGE,{"derivedFrom":[makeQuery(id+"F5.boolean.opBoolean","COPY",FACE,{"derivedFrom":makeQuery(id+"F5.opExtrude","SWEPT_FACE",FACE,{"disambiguationData":[OSD([sQuery(id+"F2.wireOp",EDGE,"E12")])]})}),makeQuery(id+"F9.opExtrude","SWEPT_FACE",FACE,{"disambiguationData":[OSD([sQuery(id+"F7.wireOp",EDGE,"E27.filletArc")])]})]}),"instanceName":"1"});
            var Q3;
            Q3=makeQuery(id+"F23.opPattern","COPY",EDGE,{"derivedFrom":makeQuery(id+"F9.boolean.opBoolean","INTERSECT",EDGE,{"derivedFrom":[makeQuery(id+"F5.boolean.opBoolean","COPY",FACE,{"derivedFrom":makeQuery(id+"F5.opExtrude","SWEPT_FACE",FACE,{"disambiguationData":[OSD([sQuery(id+"F2.wireOp",EDGE,"E12")])]})}),makeQuery(id+"F9.opExtrude","SWEPT_FACE",FACE,{"disambiguationData":[OSD([sQuery(id+"F7.wireOp",EDGE,"E26")])]})]}),"instanceName":"1"});
            var Q4;
            {var subQ1=makeQuery(id+"F9.opExtrude","SWEPT_FACE",FACE,{"disambiguationData":[OSD([sQuery(id+"F7.wireOp",EDGE,"E24")])]});var subQ2=makeQuery(id+"F3.boolean.opBoolean","COPY",FACE,{"derivedFrom":makeQuery(id+"F3.opExtrude","SWEPT_FACE",FACE,{"disambiguationData":[OSD([sQuery(id+"F2.wireOp",EDGE,"E14")])]})});Q4=makeQuery(id+"F23.opPattern","COPY",EDGE,{"derivedFrom":makeQuery(id+"F11.boolean.opBoolean","SPLIT",EDGE,{"disambiguationData":[TD([makeQuery(id+"F9.boolean.opBoolean","COPY",FACE,{"derivedFrom":makeQuery(id+"F9.opExtrude","SWEPT_FACE",FACE,{"disambiguationData":[OSD([sQuery(id+"F7.wireOp",EDGE,"E25")])]})})])],"derivedFrom":makeQuery(id+"F9.boolean.opBoolean","INTERSECT",EDGE,{"derivedFrom":[subQ2,subQ1]})}),"instanceName":"1"});}
            fillet(context, id + "F31", {"entities" : qUnion([Q0, Q1, Q2, Q3, Q4]), "radius" : 0.3 * mm, "tangentPropagation" : true, "allowEdgeOverflow" : false});
        }
    });
